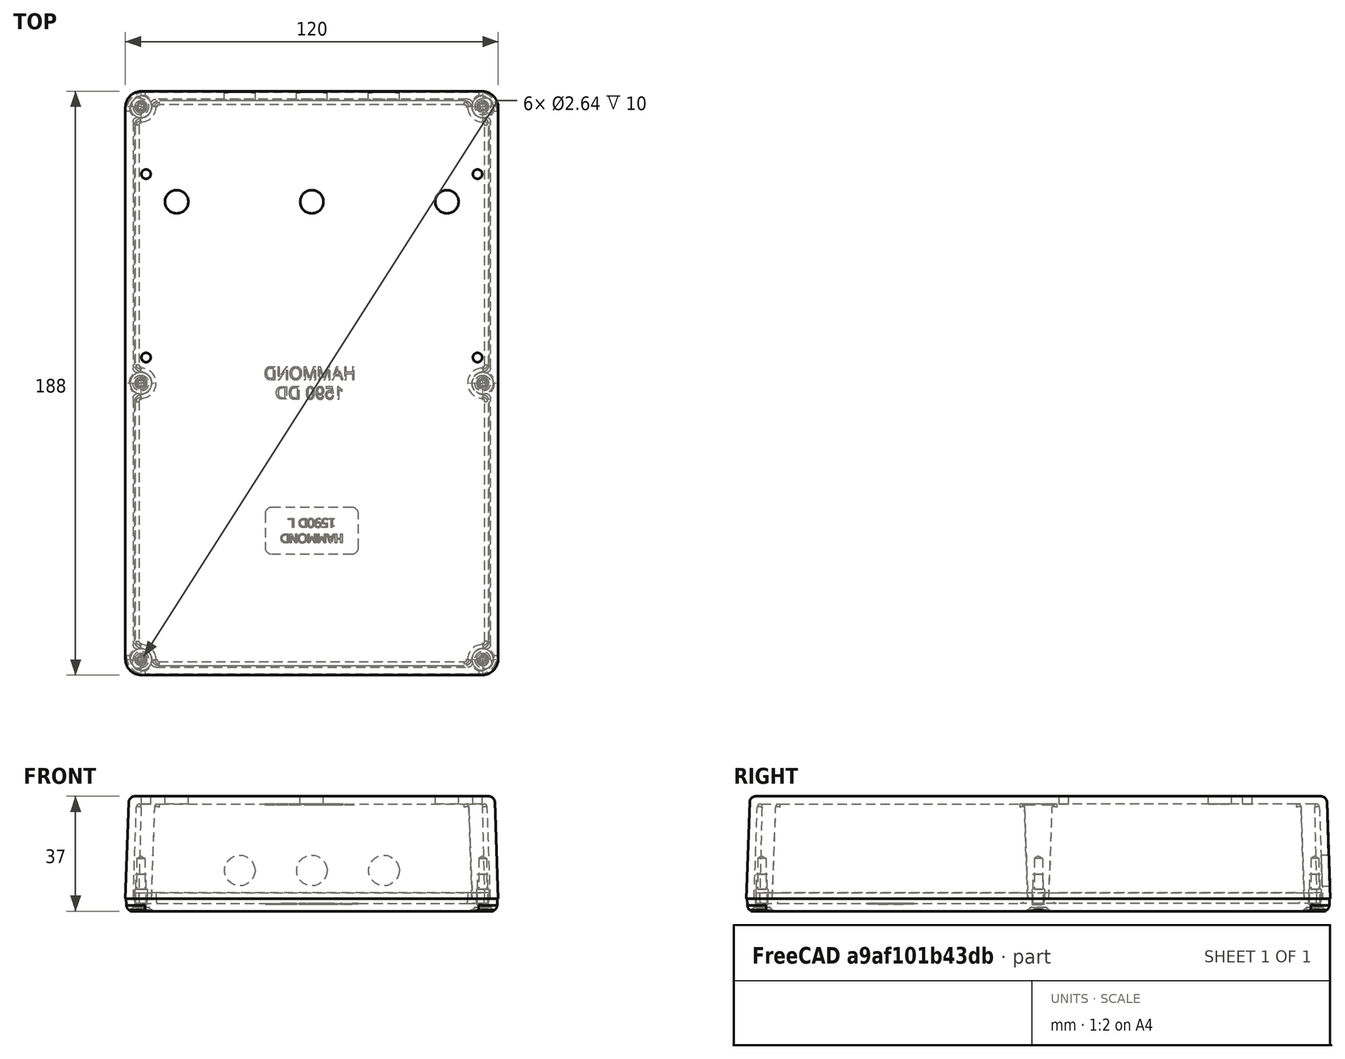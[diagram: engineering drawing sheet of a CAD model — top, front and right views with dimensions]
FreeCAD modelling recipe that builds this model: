
FCSTD DOCUMENT  (FreeCAD 0.18R16131 (Git))
Label: #700-000 - Enclosure [Parts]
License: All rights reserved
LicenseURL: http://en.wikipedia.org/wiki/All_rights_reserved
objects: Part::Cylinder×10, PartDesign::ShapeBinder×9, Part::Feature×8, PartDesign::Plane×5, App::Part×4, Part::MultiFuse×2, Part::Cut×1, PartDesign::Body×1
note: 36 computed .brp shape members not serialized (recipe doc carries the construction recipe); baked Part::Feature solids carry a one-line shape summary decoded from their .brp

FEATURE [PartDesign::Plane] DatumPlane  label="Origin_XY_DatumPlane"
  AttachmentOffset = pos=(-75,-100,0) rot=(0,0,1;0rad)
  Length = 150
  MapMode = 5
  Placement = pos=(-75,-100,0) rot=(0,0,1;0rad)
  ResizeMode = 1
  Support = -> [XY_Plane001]
  Width = 200
FEATURE [Part::Feature] Part__Feature  label="#700-001 - 1590DD Box"
  Placement = pos=(0,0,0) rot=(0.707107,0.707107,0;3.14159rad)
  shape: bbox 120 x 188 x 451.1 mm, 273 faces (baked)
FEATURE [Part::Feature] Part__Feature001  label="#700-001 - 1590DD - Lid"
  Placement = pos=(0,0,0) rot=(0,0.707107,0.707107;3.14159rad)
  shape: bbox 187.5 x 5.937 x 119.5 mm, 345 faces (baked)
FEATURE [Part::Feature] Part__Feature002  label="#700-001 - 1590DD - Screw 4/6"
  Placement = pos=(1.2e-14,1.5362,-55) rot=(0,1,0;0.650238rad)
  shape: bbox 6.871 x 11.85 x 6.871 mm, 25 faces (baked)
FEATURE [Part::Feature] Part__Feature003  label="#700-001 - 1590DD - Screw 2/6"
  Placement = pos=(-1.2e-14,1.5362,55) rot=(0,1,0;0.650238rad)
  shape: bbox 6.871 x 11.85 x 6.871 mm, 25 faces (baked)
FEATURE [Part::Feature] Part__Feature004  label="#700-001 - 1590DD - Screw 1/6"
  Placement = pos=(-89,1.5362,55) rot=(0,1,0;0.650238rad)
  shape: bbox 6.871 x 11.85 x 6.871 mm, 25 faces (baked)
FEATURE [Part::Feature] Part__Feature005  label="#700-001 - 1590DD - Screw 3/6"
  Placement = pos=(-89,1.5362,-55) rot=(0,-1,0;0.529817rad)
  shape: bbox 6.871 x 11.85 x 6.871 mm, 25 faces (baked)
FEATURE [Part::Feature] Part__Feature006  label="#700-001 - 1590DD - Screw 5/6"
  Placement = pos=(89,1.5362,55) rot=(0,0,1;0rad)
  shape: bbox 6.871 x 11.85 x 6.871 mm, 25 faces (baked)
FEATURE [Part::Feature] Part__Feature007  label="#700-001 - 1590DD - Screw 6/6"
  Placement = pos=(89,1.5362,-55) rot=(0,0,1;0rad)
  shape: bbox 6.871 x 11.85 x 6.871 mm, 25 faces (baked)
FEATURE [Part::MultiFuse] Fusion  label="#700-000 - Enclosure - Lid & Screws, Fusion"
  Placement = pos=(0,0,0) rot=(0.57735,-0.57735,0.57735;4.18879rad)
  Shapes = -> [Part__Feature001,Part__Feature004,Part__Feature003,Part__Feature005,Part__Feature002,Part__Feature006,Part__Feature007]
FEATURE [Part::Cylinder] Cylinder  label="Drill - Potentiometer - Rate [D=7.5, X=-43.5, Y=58.42]"
  Angle = 360
  AttacherType = Attacher::AttachEngine3D
  Height = 10
  Placement = pos=(-43.498,58.42,25) rot=(0,0,1;0rad)
  Radius = 3.75
FEATURE [Part::Cylinder] Cylinder001  label="Drill - Potentiometer - Depth [D7.5, X=0.0, Y = 58.42]]"
  Angle = 360
  AttacherType = Attacher::AttachEngine3D
  Height = 10
  Placement = pos=(0,58.42,25) rot=(0,0,1;0rad)
  Radius = 3.75
FEATURE [Part::Cylinder] Cylinder002  label="Drill - Potentiometer - Feedback [D=7.5, X=43.5, Y=58.42]"
  Angle = 360
  AttacherType = Attacher::AttachEngine3D
  Height = 10
  Placement = pos=(43.498,58.42,25) rot=(0,0,1;0rad)
  Radius = 3.75
FEATURE [PartDesign::Plane] DatumPlane001  label="Enclosure_Face_XY_DatumPlane"
  Length = 104.339
  MapMode = 5
  Placement = pos=(0,0,30.5) rot=(1,0,0;3.14159rad)
  ResizeMode = 0
  Width = 129.339
FEATURE [Part::Cylinder] Cylinder003  label="Drill - Standoff 4/4 [D=3.0, X=-53.34, Y=8.26]"
  Angle = 360
  AttacherType = Attacher::AttachEngine3D
  Height = 10
  Placement = pos=(-53.34,8.26,26) rot=(0,0,1;0rad)
  Radius = 1.5
FEATURE [Part::Cylinder] Cylinder004  label="Drill - Standoff 3/4 [D=3.0, X=53.34, Y=8.26]"
  Angle = 360
  AttacherType = Attacher::AttachEngine3D
  Height = 10
  Placement = pos=(53.34,8.26,26) rot=(0,0,1;0rad)
  Radius = 1.5
FEATURE [Part::Cylinder] Cylinder005  label="Drill - Standoff 2/4 [D=3.0, X=-53.34, Y=67.31]"
  Angle = 360
  AttacherType = Attacher::AttachEngine3D
  Height = 10
  Placement = pos=(-53.34,67.31,26) rot=(0,0,1;0rad)
  Radius = 1.5
FEATURE [Part::Cylinder] Cylinder006  label="Drill - Standoff 1/4 [D=3.0, X=53.34, Y=67.31]"
  Angle = 360
  AttacherType = Attacher::AttachEngine3D
  Height = 10
  Placement = pos=(53.34,67.31,26) rot=(0,0,1;0rad)
  Radius = 1.5
FEATURE [App::Part] Part001  label="#700-000 - Enclosure - Lid & Screws"
  Group = -> [Part__Feature004,Part__Feature007,Part__Feature005,Part__Feature001,Part__Feature003,Part__Feature006,Part__Feature002,Fusion]
  Origin = -> Origin002
FEATURE [PartDesign::ShapeBinder] ShapeBinder  label="Enclosure_Lid_Inside"
  Placement = pos=(0,0,0) rot=(0.707107,0.707107,0;3.14159rad)
  Support = -> [Fusion]
  TraceSupport = false
FEATURE [PartDesign::ShapeBinder] ShapeBinder001  label="Enclosure_Lid_Lip"
  Placement = pos=(0,0,0) rot=(0.707107,0.707107,0;3.14159rad)
  Support = -> [Fusion]
  TraceSupport = false
FEATURE [PartDesign::ShapeBinder] ShapeBinder002  label="Enclosure_Lid_Outside"
  Placement = pos=(0,0,0) rot=(0.707107,0.707107,0;3.14159rad)
  Support = -> [Fusion]
  TraceSupport = false
FEATURE [PartDesign::ShapeBinder] ShapeBinder003  label="Enclosure_Box_Top_Outside"
  Placement = pos=(0,0,0) rot=(0.707107,0.707107,0;3.14159rad)
  Support = -> [Part__Feature]
  TraceSupport = false
FEATURE [PartDesign::ShapeBinder] ShapeBinder004  label="Enclosure_Box_Top_Inside"
  Placement = pos=(0,0,0) rot=(0.707107,0.707107,0;3.14159rad)
  Support = -> [Part__Feature]
  TraceSupport = false
FEATURE [PartDesign::ShapeBinder] ShapeBinder005  label="Enclosure_Box_Rear_Outside"
  Placement = pos=(0,0,0) rot=(0.707107,0.707107,0;3.14159rad)
  Support = -> [Part__Feature]
  TraceSupport = false
FEATURE [PartDesign::ShapeBinder] ShapeBinder006  label="Enclosure_Box_Rear_Inside"
  Placement = pos=(0,0,0) rot=(0.707107,0.707107,0;3.14159rad)
  Support = -> [Part__Feature]
  TraceSupport = false
FEATURE [PartDesign::ShapeBinder] ShapeBinder007  label="Enclosure_Box_Front_Outside"
  Placement = pos=(0,0,0) rot=(0.707107,0.707107,0;3.14159rad)
  Support = -> [Part__Feature]
  TraceSupport = false
FEATURE [PartDesign::ShapeBinder] ShapeBinder008  label="Enclosure_Box_Front_Inside"
  Placement = pos=(0,0,0) rot=(0.707107,0.707107,0;3.14159rad)
  Support = -> [Part__Feature]
  TraceSupport = false
FEATURE [Part::Cylinder] Cylinder007  label="Drill - Audio Jack 1/2 [D=10.0, X=-23.2, Z=9.1]"
  Angle = 360
  AttacherType = Attacher::AttachEngine3D
  Height = 10
  Placement = pos=(-23.2,90,9.1) rot=(-1,0,0;1.5708rad)
  Radius = 5
  expr: Placement.Base.z = 1 + 1.6 + 6.5
FEATURE [Part::Cylinder] Cylinder008  label="Drill - Audio Jack 2/2 [D=10.0, X=23.2, Z=9.1]"
  Angle = 360
  AttacherType = Attacher::AttachEngine3D
  Height = 10
  Placement = pos=(23.2,90,9.1) rot=(-1,0,0;1.5708rad)
  Radius = 5
  expr: Placement.Base.z = 1 + 1.6 + 6.5
FEATURE [Part::Cylinder] Cylinder009  label="Drill - Power Jack [D=8.0, X=0.0, Y=9.1]"
  Angle = 360
  AttacherType = Attacher::AttachEngine3D
  Height = 10
  Placement = pos=(0,90,9.1) rot=(-1,0,0;1.5708rad)
  Radius = 5
FEATURE [Part::MultiFuse] Fusion001  label="Drills"
  Shapes = -> [Cylinder,Cylinder002,Cylinder001,Cylinder003,Cylinder004,Cylinder005,Cylinder006,Cylinder007,Cylinder008,Cylinder009]
FEATURE [Part::Cut] Cut  label="#700-000 - Enclosure - Box, Drilled"
  Base = -> Part__Feature
  Tool = -> Fusion001
FEATURE [App::Part] Part002  label="#700-000 - Enclosure - Box"
  Group = -> [Part__Feature,Fusion001,Cylinder002,Cylinder006,Cylinder004,Cylinder005,Cylinder,Cylinder001,Cylinder003,Cut]
  Origin = -> Origin003
FEATURE [PartDesign::Plane] DatumPlane002  label="DatumPlane_Rear_Inside"
  Length = 94.0006
  MapMode = 5
  Placement = pos=(2.03e-14,91.387,3.19131) rot=(0,0.71934,-0.694658;3.14159rad)
  ResizeMode = 0
  Support = -> [ShapeBinder006]
  Width = 32.8274
FEATURE [PartDesign::Plane] DatumPlane003  label="DatumPlane_Top_Inside"
  Length = 129.339
  MapMode = 5
  Placement = pos=(0,0,30.5) rot=(0.707107,0.707107,0;3.14159rad)
  ResizeMode = 0
  Support = -> [ShapeBinder004]
  Width = 104.339
FEATURE [PartDesign::Plane] DatumPlane004  label="DatumPlane_Lid_Inside"
  Length = 129.339
  MapMode = 5
  Placement = pos=(0,0,-1.5) rot=(0,0,1;1.5708rad)
  ResizeMode = 0
  Support = -> [ShapeBinder]
  Width = 104.339
FEATURE [PartDesign::Body] Body  label="Datum References"
  Group = -> [DatumPlane,DatumPlane001,ShapeBinder,ShapeBinder001,ShapeBinder002,ShapeBinder003,ShapeBinder004,ShapeBinder005,ShapeBinder006,ShapeBinder007,ShapeBinder008,DatumPlane002,DatumPlane003,DatumPlane004]
  Origin = -> Origin001
FEATURE [App::Part] Part003  label="#700-000 - Datum References"
  Group = -> [Body]
  Origin = -> Origin004
FEATURE [App::Part] Part  label="#700-000 - Enclosure"
  Group = -> [Part001,Part002,Part003]
  Origin = -> Origin
